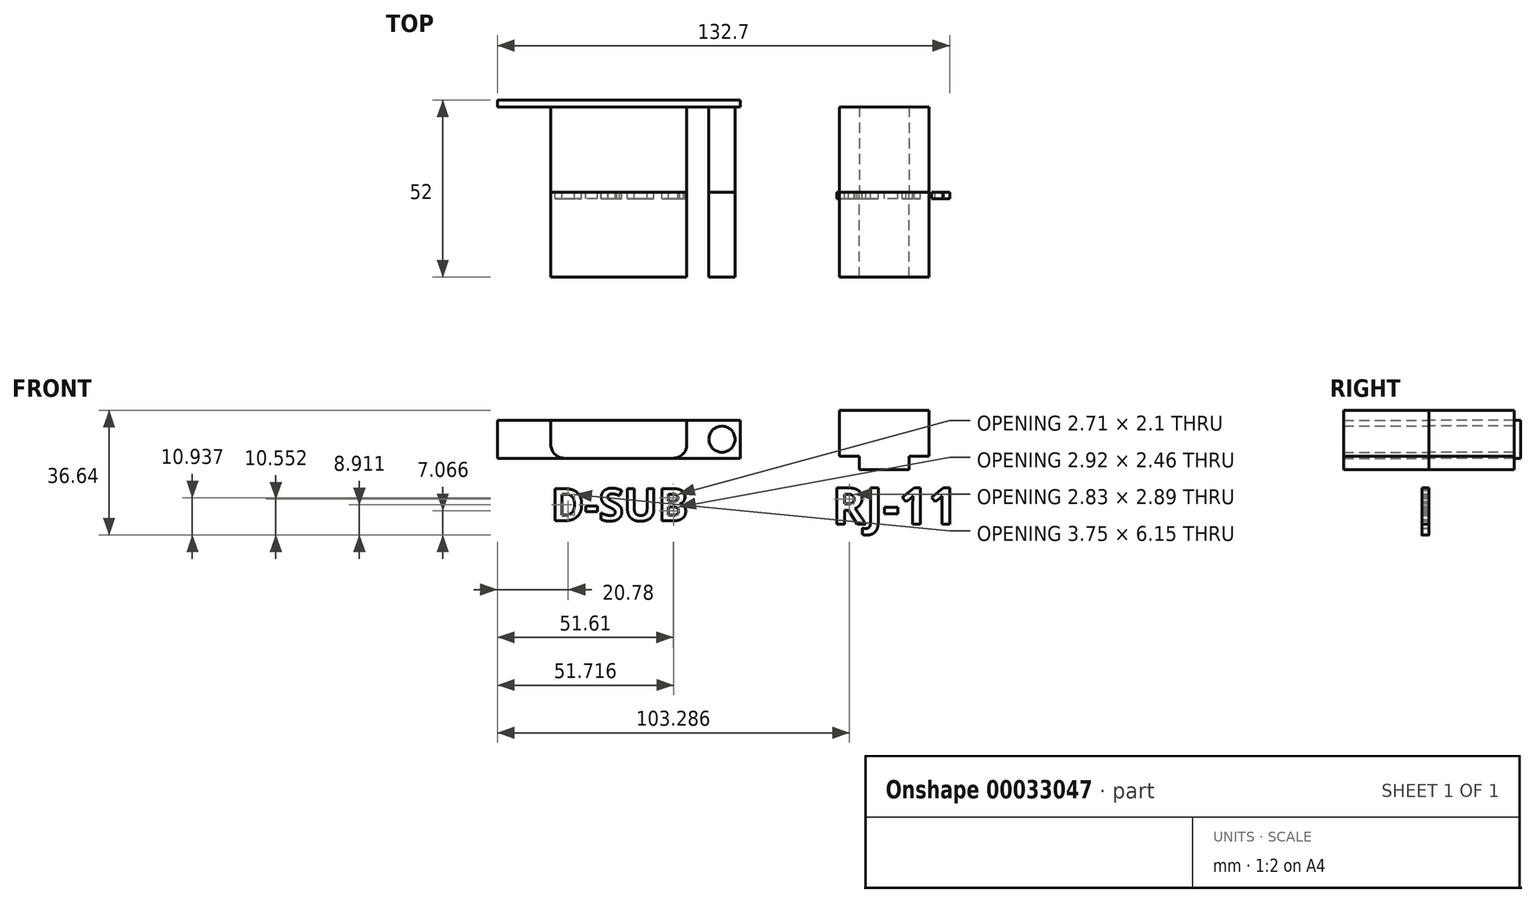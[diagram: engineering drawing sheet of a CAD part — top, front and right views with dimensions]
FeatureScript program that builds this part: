
annotation { "Feature Type Name" : "Feature", "Feature Type Description" : "" }
export const myFeature = defineFeature(function(context is Context, id is Id, definition is map)
    precondition{}
    {
        {
            var Q0;
            Q0=qCreatedBy(makeId("Front.planeOp"),FACE);
            cPlane(context, id + "F0", {"entities" : qUnion([Q0]), "cplaneType" : CPlaneType.OFFSET, "offset" : 0 * mm, "width" : 150 * mm, "height" : 150 * mm});
        }
        {
            var Q0;
            Q0=qCreatedBy(id+"F0.planeOp",FACE);
            cPlane(context, id + "F1", {"entities" : qUnion([Q0]), "cplaneType" : CPlaneType.OFFSET, "offset" : 0 * mm, "width" : 150 * mm, "height" : 150 * mm});
        }
        {
            var Q0;
            Q0=qCreatedBy(makeId("Front.planeOp"),FACE);
            var sketch = newSketch(context, id + "F2", { "sketchPlane" : qUnion([Q0])});
            skLineSegment(sketch, "E0.bottom", {"start": v(-209.53, 99.03) * mm, "end": v(-169.62, 99.03) * mm});
            skLineSegment(sketch, "E0.top", {"start": v(-205.53, 87.86) * mm, "end": v(-173.62, 87.86) * mm});
            skLineSegment(sketch, "E0.left", {"start": v(-209.53, 99.03) * mm, "end": v(-209.53, 91.86) * mm});
            skLineSegment(sketch, "E0.right", {"start": v(-169.62, 99.03) * mm, "end": v(-169.62, 91.86) * mm});
            skCircle(sketch, "E1", {"center": v(-159.31, 93.45) * mm, "radius": 3.83 * mm});
            skPoint(sketch, "E2", {"position": v(-189.58, 93.45) * mm});
            skCircle(sketch, "E3.MirrorC", {"center": v(-219.84, 93.45) * mm, "radius": 3.83 * mm});
            skLineSegment(sketch, "E4", {"start": v(-189.58, 93.45) * mm, "end": v(-159.31, 93.45) * mm, "construction": true});
            skLineSegment(sketch, "E5", {"start": v(-189.58, 93.45) * mm, "end": v(-219.84, 93.45) * mm, "construction": true});
            skLineSegment(sketch, "E6", {"start": v(-189.58, 93.45) * mm, "end": v(-189.58, 87.86) * mm, "construction": true});
            skLineSegment(sketch, "E7", {"start": v(-189.58, 93.45) * mm, "end": v(-189.58, 99.03) * mm, "construction": true});
            skPoint(sketch, "E8.visualSharp", {"position": v(-209.53, 87.86) * mm});
            skArc(sketch, "E8.filletArc", {"start": v(-209.53, 91.86) * mm, "mid": v(-208.36, 89.03) * mm, "end": v(-205.53, 87.86) * mm});
            skPoint(sketch, "E9.visualSharp", {"position": v(-169.62, 87.86) * mm});
            skArc(sketch, "E9.filletArc", {"start": v(-173.62, 87.86) * mm, "mid": v(-170.8, 89.03) * mm, "end": v(-169.62, 91.86) * mm});
            skSolve(sketch);
        }
        {
            var Q0;
            Q0=qCreatedBy(id+"F0.planeOp",FACE);
            var sketch = newSketch(context, id + "F3", { "sketchPlane" : qUnion([Q0])});
            skLineSegment(sketch, "E10", {"start": v(-111.67, 101.96) * mm, "end": v(-111.67, 93.27) * mm, "construction": true});
            skLineSegment(sketch, "E11", {"start": v(-111.67, 93.27) * mm, "end": v(-111.67, 84.57) * mm, "construction": true});
            skLineSegment(sketch, "E12", {"start": v(-111.67, 101.96) * mm, "end": v(-98.56, 101.96) * mm});
            skLineSegment(sketch, "E13", {"start": v(-98.56, 101.96) * mm, "end": v(-98.56, 88.47) * mm});
            skLineSegment(sketch, "E14", {"start": v(-98.56, 88.47) * mm, "end": v(-104.36, 88.47) * mm});
            skLineSegment(sketch, "E15", {"start": v(-104.36, 88.47) * mm, "end": v(-104.36, 84.57) * mm});
            skLineSegment(sketch, "E16", {"start": v(-104.36, 84.57) * mm, "end": v(-111.67, 84.57) * mm});
            skLineSegment(sketch, "E17.MirrorCS", {"start": v(-111.67, 101.96) * mm, "end": v(-124.78, 101.96) * mm});
            skLineSegment(sketch, "E18.MirrorCS", {"start": v(-124.78, 101.96) * mm, "end": v(-124.78, 88.47) * mm});
            skLineSegment(sketch, "E19.MirrorCS", {"start": v(-124.78, 88.47) * mm, "end": v(-118.98, 88.47) * mm});
            skLineSegment(sketch, "E20.MirrorCS", {"start": v(-118.98, 88.47) * mm, "end": v(-118.98, 84.57) * mm});
            skLineSegment(sketch, "E21.MirrorCS", {"start": v(-118.98, 84.57) * mm, "end": v(-111.67, 84.57) * mm});
            skPoint(sketch, "E22", {"position": v(16.04, -19) * mm});
            skSolve(sketch);
        }
        {
            var Q0;
            Q0=qCreatedBy(id+"F1.planeOp",FACE);
            var sketch = newSketch(context, id + "F4", { "sketchPlane" : qUnion([Q0])});
            skText(sketch, "E23", { "text": "D-SUB", "fontName": "OpenSans-Bold.ttf"});
            const initialGuessF4  = {"E23": [-0.2095, 0.0695, 1, 0, 0.00953]};
            skSetInitialGuess(sketch, initialGuessF4);
            skSolve(sketch);
        }
        {
            var Q0;
            Q0=qCreatedBy(id+"F0.planeOp",FACE);
            var sketch = newSketch(context, id + "F5", { "sketchPlane" : qUnion([Q0])});
            skText(sketch, "E24", { "text": "RJ-11", "fontName": "OpenSans-Bold.ttf"});
            const initialGuessF5  = {"E24": [-0.12696, 0.06847, 1, 0, 0.0108]};
            skSetInitialGuess(sketch, initialGuessF5);
            skSolve(sketch);
        }
        {
            var Q0;
            Q0 = qSketchRegion(id + "F4", true);
            extrude(context, id + "F6", {"entities" : qUnion([Q0]), "depth" : 2 * mm});
        }
        {
            var Q0;
            Q0 = qSketchRegion(id + "F5", true);
            extrude(context, id + "F7", {"entities" : qUnion([Q0]), "depth" : 2 * mm});
        }
        {
            var Q0;
            Q0=makeQuery(id+"F3.imprint","IMPRINT",FACE,{"disambiguationData":[TD([[makeQuery(id+"F3.imprint","IMPRINT",EDGE,{"derivedFrom":sQuery(id+"F3.wireOp",EDGE,"E12")}),-1.0]])]});
            extrude(context, id + "F8", {"entities" : qUnion([Q0]), "oppositeDirection" : true, "depth" : 25 * mm});
        }
        {
            var Q0;
            Q0=makeQuery(id+"F8.opExtrude","SWEPT_BODY",BODY,{"disambiguationData":[OSD([sQuery(id+"F3.wireOp",EDGE,"E12"),sQuery(id+"F3.wireOp",EDGE,"E13"),sQuery(id+"F3.wireOp",EDGE,"E14"),sQuery(id+"F3.wireOp",EDGE,"E15"),sQuery(id+"F3.wireOp",EDGE,"E16"),sQuery(id+"F3.wireOp",EDGE,"E17.MirrorCS"),sQuery(id+"F3.wireOp",EDGE,"E18.MirrorCS"),sQuery(id+"F3.wireOp",EDGE,"E19.MirrorCS"),sQuery(id+"F3.wireOp",EDGE,"E20.MirrorCS"),sQuery(id+"F3.wireOp",EDGE,"E21.MirrorCS")])]});
            var Q1;
            Q1=makeQuery(id+"F8.opExtrude","CAP_FACE",FACE,{"disambiguationData":[OSD([sQuery(id+"F3.wireOp",EDGE,"E12"),sQuery(id+"F3.wireOp",EDGE,"E13"),sQuery(id+"F3.wireOp",EDGE,"E14"),sQuery(id+"F3.wireOp",EDGE,"E15"),sQuery(id+"F3.wireOp",EDGE,"E16"),sQuery(id+"F3.wireOp",EDGE,"E17.MirrorCS"),sQuery(id+"F3.wireOp",EDGE,"E18.MirrorCS"),sQuery(id+"F3.wireOp",EDGE,"E19.MirrorCS"),sQuery(id+"F3.wireOp",EDGE,"E20.MirrorCS"),sQuery(id+"F3.wireOp",EDGE,"E21.MirrorCS")])],"isStart":true});
            mirror(context, id + "F9", {"operationType" : NewBodyOperationType.ADD, "entities" : qUnion([Q0]), "mirrorPlane" : qUnion([Q1])});
        }
        {
            var Q0;
            Q0=makeQuery(id+"F2.imprint","IMPRINT",FACE,{"disambiguationData":[TD([[makeQuery(id+"F2.imprint","IMPRINT",EDGE,{"derivedFrom":sQuery(id+"F2.wireOp",EDGE,"E3.MirrorC")}),-1.0]])]});
            var Q1;
            Q1=makeQuery(id+"F2.imprint","IMPRINT",FACE,{"disambiguationData":[TD([[makeQuery(id+"F2.imprint","IMPRINT",EDGE,{"derivedFrom":sQuery(id+"F2.wireOp",EDGE,"E0.bottom")}),-1.0]])]});
            var Q2;
            Q2=makeQuery(id+"F2.imprint","IMPRINT",FACE,{"disambiguationData":[TD([[makeQuery(id+"F2.imprint","IMPRINT",EDGE,{"derivedFrom":sQuery(id+"F2.wireOp",EDGE,"E1")}),1.0]])]});
            extrude(context, id + "F10", {"entities" : qUnion([Q0, Q1, Q2]), "oppositeDirection" : true, "depth" : 25 * mm});
        }
        {
            var Q0;
            Q0=makeQuery(id+"F10.opExtrude","SWEPT_BODY",BODY,{"disambiguationData":[OSD([sQuery(id+"F2.wireOp",EDGE,"E1")])]});
            var Q1;
            Q1=makeQuery(id+"F10.opExtrude","SWEPT_BODY",BODY,{"disambiguationData":[OSD([sQuery(id+"F2.wireOp",EDGE,"E0.bottom"),sQuery(id+"F2.wireOp",EDGE,"E0.top"),sQuery(id+"F2.wireOp",EDGE,"E0.left"),sQuery(id+"F2.wireOp",EDGE,"E0.right")])]});
            var Q2;
            Q2=makeQuery(id+"F10.opExtrude","SWEPT_BODY",BODY,{"disambiguationData":[OSD([sQuery(id+"F2.wireOp",EDGE,"E3.MirrorC")])]});
            var Q3;
            Q3=makeQuery(id+"F10.opExtrude","CAP_FACE",FACE,{"disambiguationData":[OSD([sQuery(id+"F2.wireOp",EDGE,"E0.bottom"),sQuery(id+"F2.wireOp",EDGE,"E0.top"),sQuery(id+"F2.wireOp",EDGE,"E0.left"),sQuery(id+"F2.wireOp",EDGE,"E0.right")])],"isStart":true});
            mirror(context, id + "F11", {"operationType" : NewBodyOperationType.ADD, "entities" : qUnion([Q0, Q1, Q2]), "mirrorPlane" : qUnion([Q3])});
        }
        {
            var Q0;
            Q0=makeQuery(id+"F10.opExtrude","CAP_FACE",FACE,{"disambiguationData":[OSD([sQuery(id+"F2.wireOp",EDGE,"E0.bottom"),sQuery(id+"F2.wireOp",EDGE,"E0.top"),sQuery(id+"F2.wireOp",EDGE,"E0.left"),sQuery(id+"F2.wireOp",EDGE,"E0.right")])],"isStart":false});
            var sketch = newSketch(context, id + "F12", { "sketchPlane" : qUnion([Q0])});
            skLineSegment(sketch, "E25.0.0", {"start": v(209.53, 99.03) * mm, "end": v(209.53, 99.03) * mm});
            skLineSegment(sketch, "E25.0.1", {"start": v(209.53, 99.03) * mm, "end": v(169.62, 99.03) * mm});
            skLineSegment(sketch, "E25.0.2", {"start": v(169.62, 99.03) * mm, "end": v(169.62, 99.03) * mm});
            skLineSegment(sketch, "E26", {"start": v(189.58, 87.86) * mm, "end": v(189.58, 99.03) * mm, "construction": true});
            skPoint(sketch, "E27", {"position": v(189.58, 93.45) * mm});
            skArc(sketch, "E28.0.0", {"start": v(205.53, 87.86) * mm, "mid": v(208.36, 89.03) * mm, "end": v(209.53, 91.86) * mm});
            skLineSegment(sketch, "E28.0.1", {"start": v(209.53, 91.86) * mm, "end": v(209.53, 99.03) * mm});
            skLineSegment(sketch, "E28.0.3", {"start": v(169.62, 99.03) * mm, "end": v(169.62, 91.86) * mm});
            skArc(sketch, "E28.0.4", {"start": v(169.62, 91.86) * mm, "mid": v(170.8, 89.03) * mm, "end": v(173.62, 87.86) * mm});
            skLineSegment(sketch, "E28.0.5", {"start": v(173.62, 87.86) * mm, "end": v(205.53, 87.86) * mm});
            skLineSegment(sketch, "E29.bottom", {"start": v(153.94, 99.03) * mm, "end": v(225.21, 99.03) * mm});
            skLineSegment(sketch, "E29.top", {"start": v(153.94, 87.86) * mm, "end": v(225.21, 87.86) * mm});
            skLineSegment(sketch, "E29.left", {"start": v(153.94, 99.03) * mm, "end": v(153.94, 87.86) * mm});
            skLineSegment(sketch, "E29.right", {"start": v(225.21, 99.03) * mm, "end": v(225.21, 87.86) * mm});
            skSolve(sketch);
        }
        {
            var Q0;
            {var subQ0=sQuery(id+"F12.wireOp",EDGE,"E25.0.0");Q0=makeQuery(id+"F12.imprint","IMPRINT",FACE,{"disambiguationData":[TD([[makeQuery(id+"F12.imprint","IMPRINT",EDGE,{"derivedFrom":subQ0}),1.0]])]});}
            var Q1;
            {var subQ0=sQuery(id+"F12.wireOp",EDGE,"E25.0.0");Q1=makeQuery(id+"F12.imprint","IMPRINT",FACE,{"disambiguationData":[TD([[makeQuery(id+"F12.imprint","IMPRINT",EDGE,{"derivedFrom":subQ0}),-1.0]])]});}
            var Q2;
            {var subQ0=sQuery(id+"F12.wireOp",EDGE,"E25.0.2");Q2=makeQuery(id+"F12.imprint","IMPRINT",FACE,{"disambiguationData":[TD([[makeQuery(id+"F12.imprint","IMPRINT",EDGE,{"derivedFrom":subQ0}),-1.0]])]});}
            var Q3;
            {var subQ3=sQuery(id+"F12.wireOp",EDGE,"E28.0.0");Q3=makeQuery(id+"F12.imprint","IMPRINT",FACE,{"disambiguationData":[TD([[makeQuery(id+"F12.imprint","IMPRINT",EDGE,{"derivedFrom":subQ3}),-1.0]])]});}
            var Q4;
            {var subQ1=sQuery(id+"F12.wireOp",EDGE,"E28.0.0");Q4=makeQuery(id+"F12.imprint","IMPRINT",FACE,{"disambiguationData":[TD([[makeQuery(id+"F12.imprint","IMPRINT",EDGE,{"derivedFrom":subQ1}),1.0]])]});}
            var Q5;
            {var subQ1=sQuery(id+"F12.wireOp",EDGE,"E28.0.3");Q5=makeQuery(id+"F12.imprint","IMPRINT",FACE,{"disambiguationData":[TD([[makeQuery(id+"F12.imprint","IMPRINT",EDGE,{"derivedFrom":subQ1}),-1.0]])]});}
            extrude(context, id + "F13", {"entities" : qUnion([Q0, Q1, Q2, Q3, Q4, Q5]), "depth" : 2 * mm});
        }
    });
